# Revit family: QSC SPA2-60 Amplifier Front Facing Rackmount
name_source: partatom
category: Generic Models
revit_build: Autodesk Revit 2014 (Build: 20130308_1515(x64)
units: mm (PartAtom-declared; Revit-internal decimal feet)

## types (3) — shared parameters
Default Elevation = 0.000"
Depth = 9.488"
Description = 2 Channel 60 Watt/Channel Amplfier
Face Depth = 0.079"
Heat Load Active = 61
Heat Load Standby = 33
Height = 1.730"
Manufacturer = QSC Audio Products, LLC
Manufacturer URL = http://www.qscaudio.com
Model = SPA2-60
Power Standby = 24
Product Documentation Link = http://qsc.com
Regulatory Compliance = UL, CE, RoHS/WEEE, FCC Class B
Sustainability Rating = Energy Star
URL = http://qsc.com
Voltage AC = 100-240 at 50-60 Hz
Weight Dimensional (kg) = 2.3
Weight Dimensional (lb) = 6
Weight Product (kg) = 1.1
Weight Product (lb) = 3.5
Width = 8.663"

## per-type parameters (varying)
| type | Current Draw | Power Active | Power Peak | Product Page URL |
| SPA2-60 @ 100VAC | 1.5 | 90 | 150 | http://qsc.com |
| SPA2-60 @ 120VAC | 1.5 | 84 | 180 | http://qsc.com


. |
| SPA2-60 @ 230VAC | 0.7 | 138 | 161 | http://qsc.com


. |

## geometry (parser evidence)
native form markers: Sweep x10
no freeform markers — native parametric forms only
